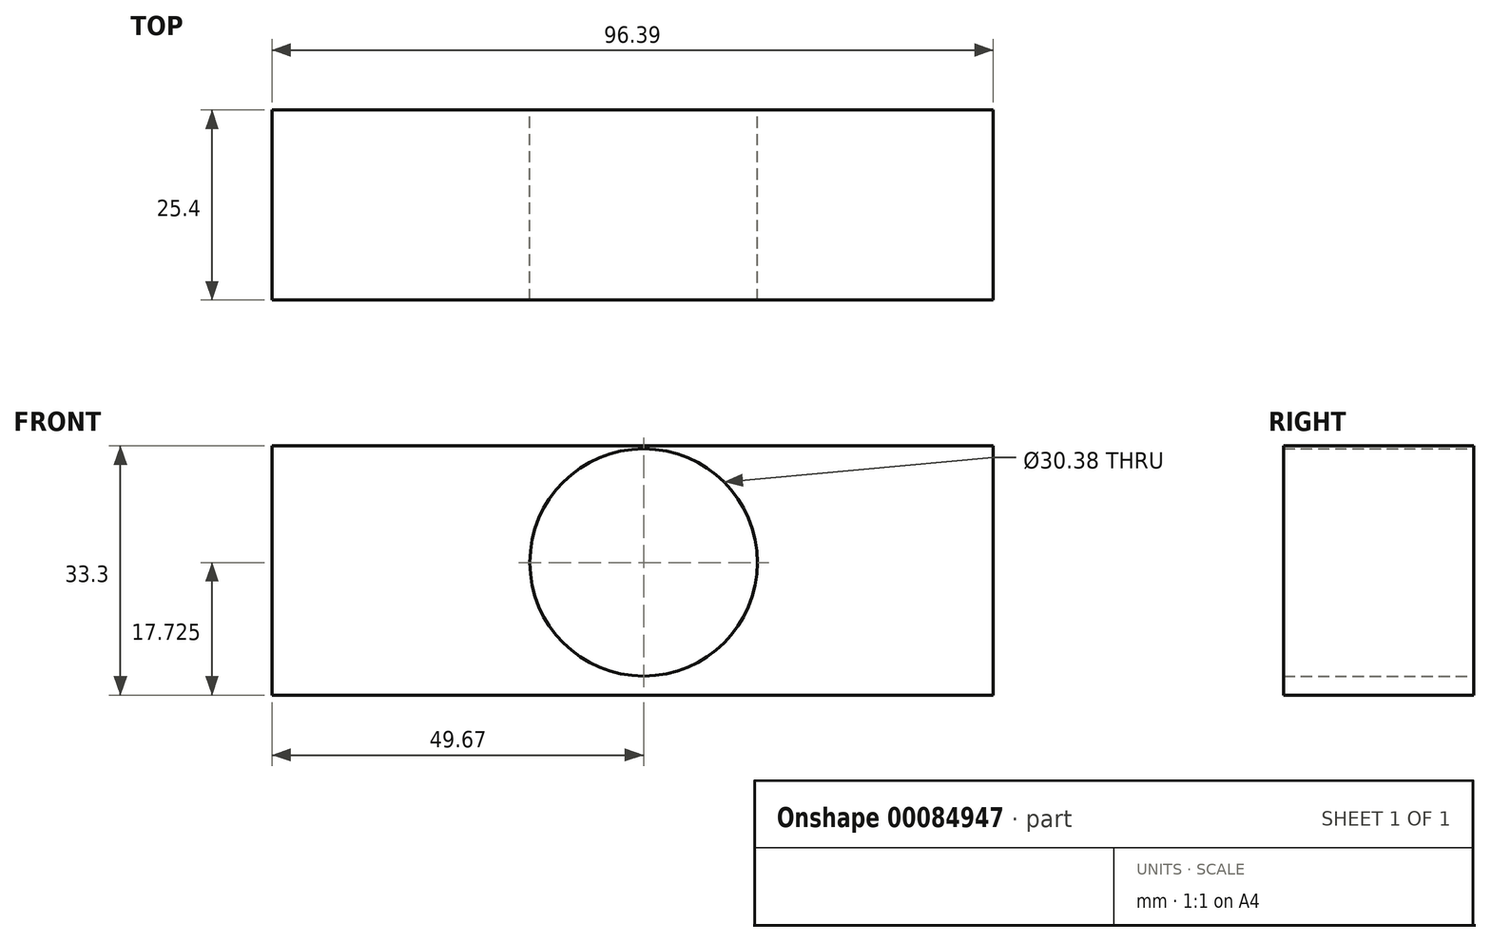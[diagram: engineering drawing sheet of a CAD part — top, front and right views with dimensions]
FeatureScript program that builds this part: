
annotation { "Feature Type Name" : "Feature", "Feature Type Description" : "" }
export const myFeature = defineFeature(function(context is Context, id is Id, definition is map)
    precondition{}
    {
        {
            var Q0;
            Q0=qCreatedBy(makeId("Front.planeOp"),FACE);
            var sketch = newSketch(context, id + "F0", { "sketchPlane" : qUnion([Q0])});
            skLineSegment(sketch, "E0.bottom", {"start": v(-49.67, 21.75) * mm, "end": v(46.72, 21.75) * mm});
            skLineSegment(sketch, "E0.top", {"start": v(-49.67, -11.55) * mm, "end": v(46.72, -11.55) * mm});
            skLineSegment(sketch, "E0.left", {"start": v(-49.67, 21.75) * mm, "end": v(-49.67, -11.55) * mm});
            skLineSegment(sketch, "E0.right", {"start": v(46.72, 21.75) * mm, "end": v(46.72, -11.55) * mm});
            skCircle(sketch, "E1", {"center": v(0, 6.18) * mm, "radius": 15.2 * mm});
            skSolve(sketch);
        }
        {
            var Q0;
            Q0 = qSketchRegion(id + "F0", true);
            extrude(context, id + "F1", {"entities" : qUnion([Q0]), "depth" : 25.4 * mm});
        }
    });
